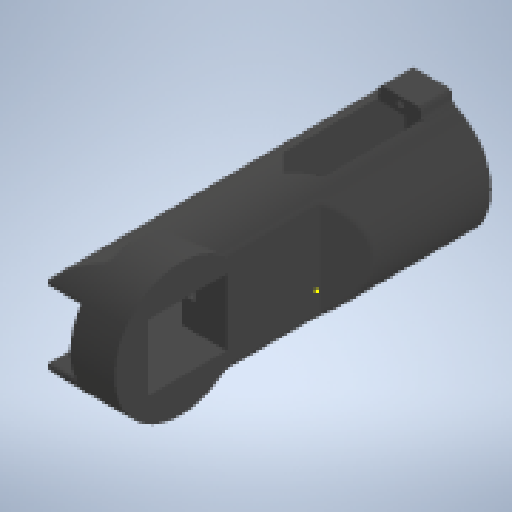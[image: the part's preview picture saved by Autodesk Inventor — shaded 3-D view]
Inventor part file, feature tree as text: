
AUTODESK INVENTOR PART (.ipt)
format: ipt  version: 2025.2 (Build 292293000, 293)  size: 889,856 bytes
history: native  units: mm
features: extrude x18, sketch x15, fillet x6, chamfer x1, plane x1, other x1
ambient origin geometry x8: Origin, YZ Plane, XZ Plane, XY Plane, X Axis, Y Axis, Z Axis, Center Point
bodies: Solid2 (feature_tree)
feature tree (42):
  extrude  "Extrusion11"  Depth=111.0mm TaperAngle=0.0deg
  extrude  "Extrusion12"  Depth=2.0mm TaperAngle=0.0deg
  extrude  "Extrusion13"  Depth=37.0mm
  extrude  "Extrusion14"  TaperAngle=0.0deg  [1 undecoded]
  extrude  "Extrusion15"  Depth=13.0mm
  extrude  "Extrusion16"  Depth=2.0mm TaperAngle=0.0deg
  fillet  "Fillet5"  Radius=7.2mm
  fillet  "Fillet6"  Radius=2.0mm
  extrude  "Extrusion17"  TaperAngle=0.0deg  [1 undecoded]
  chamfer  "Chamfer3"  Distance=10.0mm
  plane  "Work Plane3"
  extrude  "Extrusion18"  Depth=2.0mm
  extrude  "Extrusion19"  Depth=2.0mm
  sketch  "Sketch25"  dims[d184=19.1mm d185=2.0mm]
  extrude  "Extrusion20"  Depth=2.0mm TaperAngle=45.0deg
  extrude  "Extrusion21"  Depth=8.5mm TaperAngle=0.0deg
  extrude  "Extrusion22"  TaperAngle=0.0deg  [1 undecoded]
  sketch  "Sketch27"  dims[d191=65.0mm d192=8.5mm d193=0.0mm]
  extrude  "Extrusion23"  TaperAngle=0.0deg  [1 undecoded]
  extrude  "Extrusion24"  Depth=2.0mm
  extrude  "Extrusion25"  TaperAngle=0.0deg  [1 undecoded]
  extrude  "Extrusion26"  Depth=2.0mm
  fillet  "Fillet7"  Radius=25.0mm
  fillet  "Fillet8"  Radius=21.0mm
  fillet  "Fillet10"  Radius=35.5mm
  extrude  "Extrusion27"  TaperAngle=0.0deg  [1 undecoded]
  fillet  "Fillet11"  Radius=2.6mm
  other  "Plano de trabalho5"
  extrude  "Extrusão28"  Depth=2.0mm
  sketch  "Sketch15"  dims[d158=38.0mm d159=111.0mm d160=0.0mm]
  sketch  "Sketch16"  dims[d161=16.0mm d162=2.0mm d163=0.0mm]
  sketch  "Sketch17"  dims[d164=13.0mm d165=37.0mm]
  sketch  "Sketch18"  dims[d166=10.0mm d167=0.0mm d168=0.0mm]
  sketch  "Sketch19"  dims[d169=23.0mm d170=13.0mm]
  sketch  "Sketch20"  dims[d171=12.8mm d172=8.0mm d173=0.0mm d174=7.2mm d175=2.0mm]
  sketch  "Sketch21"  dims[d176=8.5mm d177=0.0mm d178=0.0mm]
  sketch  "Sketch23"  dims[d179=4.5mm d180=10.0mm d181=0.0mm]
  sketch  "Sketch24"  dims[d182=1.0mm d183=2.0mm]
  sketch  "Sketch26"  dims[d186=0.0mm d187=0.0mm d188=6.5mm d189=2.0mm d190=45.0deg]
  sketch  "Sketch28"  dims[d194=23.6mm d195=0.0mm d196=0.0mm]
  sketch  "Sketch29"  dims[d197=42.0mm d198=0.0mm d199=0.0mm]
  sketch  "Esboço30"  dims[d200=14.0mm d201=0.0mm d204=21.0mm d205=0.0mm d206=0.0mm d207=60.0mm d208=25.0mm d209=21.0mm d210=35.5mm d211=0.0mm d212=0.0mm d213=2.6mm d214=3.5mm d215=10.0mm d217=4.0mm d218=7.0mm d219=4.0mm d220=0.0mm d221=7.0mm d222=0.0mm d223=16.0mm d224=9.5mm d225=7.0mm d226=0.0mm d227=2.0mm d228=1.0mm d230=1.0mm d231=29.0mm d232=14.0mm d233=13.0mm d234=10.0mm d235=0.0mm d236=2.0mm d237=0.5mm d238=0.0mm d239=0.5mm d240=0.872665mm d241=0.5mm d242=0.872665mm]
note: 6 required parameter values undecoded (feature->parameter linkage not recoverable at this tier; creation-order binding heuristic only, values carry confidence <= 0.55)
